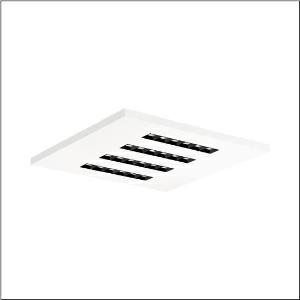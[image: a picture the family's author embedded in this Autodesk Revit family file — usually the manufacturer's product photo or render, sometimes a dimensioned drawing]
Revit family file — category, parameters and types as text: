
# Revit family: silica_r__21_square_51mx6kdu34w_c3bf
name_source: partatom
category: Lighting Fixtures
units: mm (PartAtom-declared; Revit-internal decimal feet)

## family parameters
Cut with Voids When Loaded = No
Host = Face
Light Source = No
Part Type = Normal
Room Calculation Point = No
Round Connector Dimension = Use Diameter
Shared = No

## types (1)
- --- (1 x LED, 4600 lm, 31.9 W, 3000K)
    Apparent Load = 32 VA
    CIE Flux Codes = 86 100 100 100 100
    Color Rendering = 80
    Color Temperature = 3000K
    Default Elevation = 1800 mm
    Description = Silica® 21 Square, office luminaire, primary light control with lens, of PMMA, primary anti-glare with reflector, of PC, black, CAT 2 (L<= 3000cd/m²), light emission: direct distribution, primary light characteristic: symmetric, installation type: lay-in mounting, LED, rated luminous flux: 4.600lm, luminous efficacy: 144lm/W, light colour: 830, colour temperature: 3000K, with terminal, 5-pole, mains connection: 220..240V, AC, 50/60Hz, rated input power: 31.9W, luminaire housing, of sheet steel, coated, traffic white (RAL 9016), module: M625, length: 622mm, width: 622mm, height: 33mm, protection rating (complete): IP20, insulation class (complete): insulation class I (protective earthing), certification: CE, permissible operating ambient temperature: -20..+40°C, standard: EN 50419, packaging unit: 1 piece
    Height = 0 mm  [stored 0 ft]
    Lamp = 1 x LED
    Lamp Light Flux = 4600 lm
    Lamp Power = 31.9 W
    Lamp count = 1
    Length = 622 mm
    Luminous efficacy = 144 lm/W
    Manufacturer = Siteco
    ModVariant = No
    Model = 51MX6KDU34W
    Mounting Place = Ceiling
    Mounting Type = Recessed
    Number of Poles = 1
    OnlyDefault = Yes
    Power Factor = 1
    Product Name = Silica® 21 Square
    Product group = office luminaire | ceiling recessed
    ProductGroupID = 400
    Protection Class = Protection class I
    Protection Degree = IP 20
    RLX_Detail_Level = 1
    RLX_Emergency_Light_Flux = 0 lm
    RLX_Emergency_Type = 0
    RLX_Emergency_Type_DB = No
    RlxData = <blob elided: 41957 chars, md5=ab9ea65c>
    Socket = socket
    Standby Power = 0 W
    System Light Flux = 4600 lm
    System Power = 32 W
    Type Comments = factory setting: luminous flux: 100 % | dim-lin: 254 | 430 mA
    Type Image = l_1275207.jpg
    URL = http://relux.com
    VarID = @adj_053355
    Voltage = 0 V
    Weight = 0.00 kg
    Width = 622 mm

note: [stored X ft] marks values corroborated as IEEE doubles in the binary element streams (Revit-internal decimal feet)

## geometry (parser evidence)
native form markers: Blend x4, Sweep x9
no freeform markers — native parametric forms only
